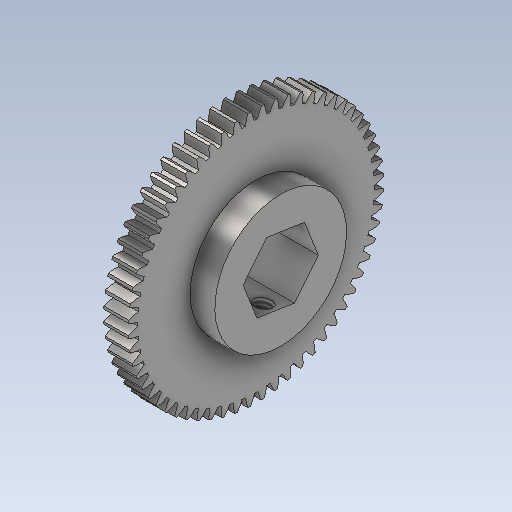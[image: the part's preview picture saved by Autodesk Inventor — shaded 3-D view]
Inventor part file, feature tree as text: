
AUTODESK INVENTOR PART (.ipt)
format: ipt  version: 2023 (Build 270158000, 158)  size: 515,584 bytes
history: native  units: in
note: dims shown in document units (in); Inventor stores cm internally (conversion verified against a paired STEP export)
features: other x3, sketch x3
ambient origin geometry x8: Origin, YZ Plane, XZ Plane, XY Plane, X Axis, Y Axis, Z Axis, Center Point
bodies: Solid1 (feature_tree)
feature tree (6):
  other  "CH-1-01-60T_Output.ipt"
  other  "Solid1::CH-1-01-60T_Output.ipt"
  other  "TaggingFeature1"
  sketch  "Sketch7"
  sketch  "Sketch6"  dims[d0=0.3937in]
  sketch  "Sketch8"
